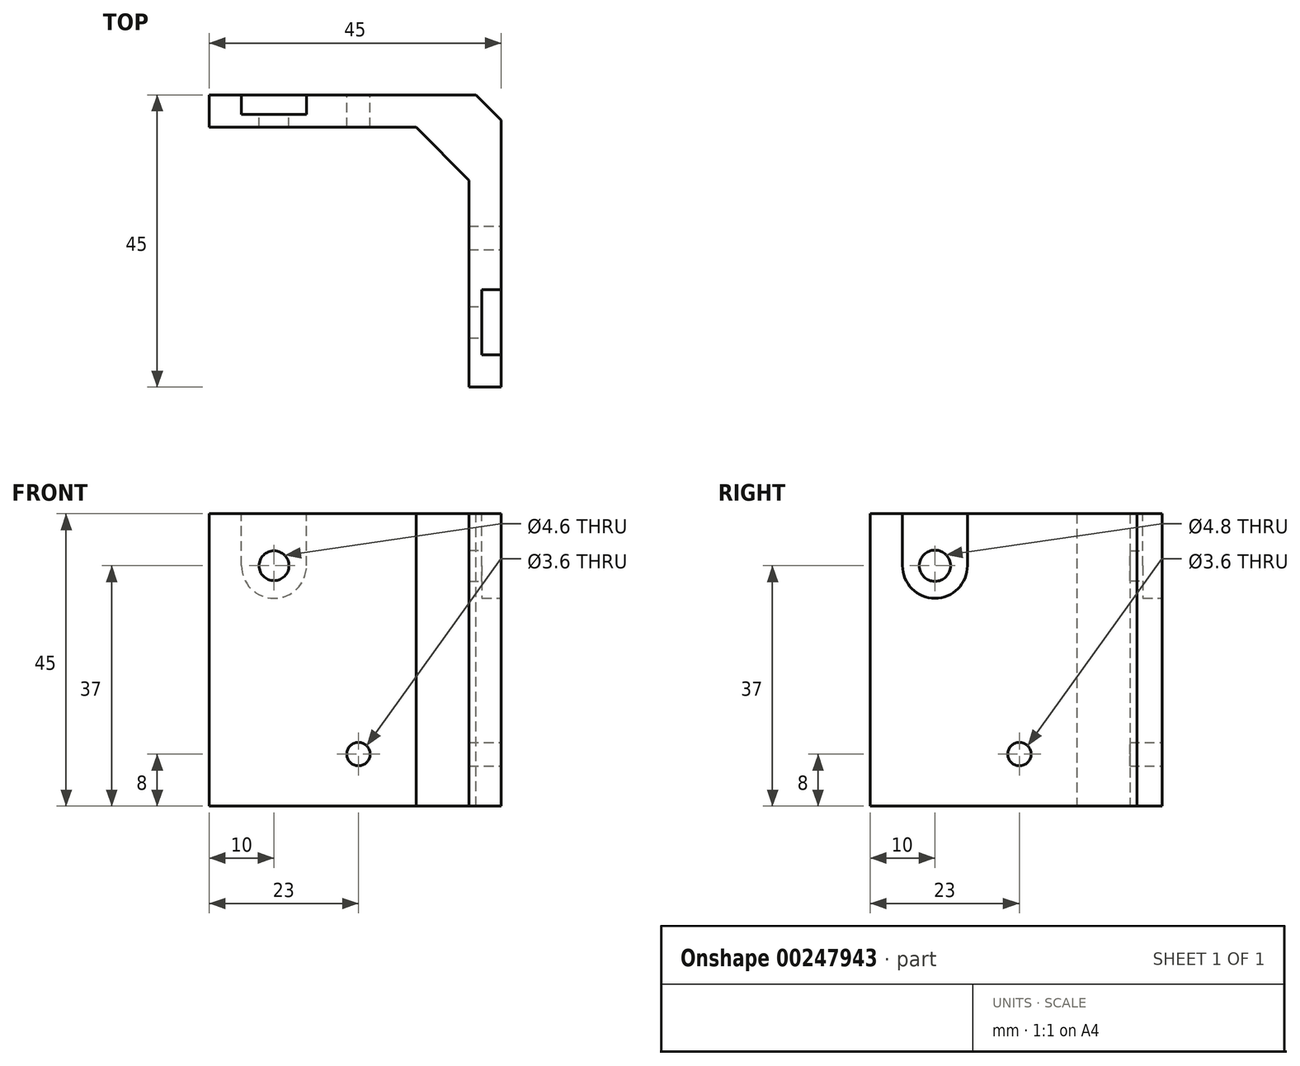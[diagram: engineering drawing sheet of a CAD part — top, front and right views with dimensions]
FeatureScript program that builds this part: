
annotation { "Feature Type Name" : "Feature", "Feature Type Description" : "" }
export const myFeature = defineFeature(function(context is Context, id is Id, definition is map)
    precondition{}
    {
        {
            var Q0;
            Q0=qCreatedBy(makeId("Top.planeOp"),FACE);
            var sketch = newSketch(context, id + "F0", { "sketchPlane" : qUnion([Q0])});
            skLineSegment(sketch, "E0.bottom", {"start": v(22.5, -22.5) * mm, "end": v(-22.5, -22.5) * mm});
            skLineSegment(sketch, "E0.top", {"start": v(22.5, 22.5) * mm, "end": v(-22.5, 22.5) * mm});
            skLineSegment(sketch, "E0.left", {"start": v(22.5, -22.5) * mm, "end": v(22.5, 22.5) * mm});
            skLineSegment(sketch, "E0.right", {"start": v(-22.5, -22.5) * mm, "end": v(-22.5, 22.5) * mm});
            skPoint(sketch, "E0.middle", {"position": v(0, 0) * mm});
            skSolve(sketch);
        }
        {
            var Q0;
            Q0 = qSketchRegion(id + "F0", true);
            extrude(context, id + "F1", {"entities" : qUnion([Q0]), "depth" : 5 * mm});
        }
        {
            var Q0;
            Q0=makeQuery(id+"F1.opExtrude","CAP_FACE",FACE,{"disambiguationData":[OSD([sQuery(id+"F0.wireOp",EDGE,"E0.bottom"),sQuery(id+"F0.wireOp",EDGE,"E0.top"),sQuery(id+"F0.wireOp",EDGE,"E0.left"),sQuery(id+"F0.wireOp",EDGE,"E0.right")])],"isStart":false});
            var sketch = newSketch(context, id + "F2", { "sketchPlane" : qUnion([Q0])});
            skLineSegment(sketch, "E1.bottom", {"start": v(-22.5, 22.5) * mm, "end": v(22.5, 22.5) * mm});
            skLineSegment(sketch, "E1.top", {"start": v(-22.5, 17.5) * mm, "end": v(22.5, 17.5) * mm});
            skLineSegment(sketch, "E1.left", {"start": v(-22.5, 22.5) * mm, "end": v(-22.5, 17.5) * mm});
            skLineSegment(sketch, "E1.right", {"start": v(22.5, 22.5) * mm, "end": v(22.5, 17.5) * mm});
            skSolve(sketch);
        }
        {
            var Q0;
            Q0=makeQuery(id+"F2.imprint","IMPRINT",FACE,{"disambiguationData":[TD([[makeQuery(id+"F2.imprint","IMPRINT",EDGE,{"derivedFrom":sQuery(id+"F2.wireOp",EDGE,"E1.bottom")}),1.0]])]});
            extrude(context, id + "F3", {"entities" : qUnion([Q0]), "operationType" : NewBodyOperationType.ADD, "depth" : 40 * mm});
        }
        {
            var Q0;
            Q0=makeQuery(id+"F3.boolean.opBoolean","MERGE",FACE,{"derivedFrom":[makeQuery(id+"F1.opExtrude","SWEPT_FACE",FACE,{"disambiguationData":[OSD([sQuery(id+"F0.wireOp",EDGE,"E0.right")])]}),makeQuery(id+"F3.opExtrude","SWEPT_FACE",FACE,{"disambiguationData":[OSD([sQuery(id+"F2.wireOp",EDGE,"E1.left")])]})]});
            var sketch = newSketch(context, id + "F4", { "sketchPlane" : qUnion([Q0])});
            skLineSegment(sketch, "E2.0", {"start": v(-17.5, 45) * mm, "end": v(-17.5, 5) * mm});
            skLineSegment(sketch, "E3.0", {"start": v(22.5, 5) * mm, "end": v(-17.5, 5) * mm});
            skLineSegment(sketch, "E4", {"start": v(-17.5, 13.13) * mm, "end": v(-9.37, 5) * mm});
            skSolve(sketch);
        }
        {
            var Q0;
            Q0 = qSketchRegion(id + "F4", true);
            var Q1;
            Q1=makeQuery(id+"F3.boolean.opBoolean","MERGE",FACE,{"derivedFrom":[makeQuery(id+"F1.opExtrude","SWEPT_FACE",FACE,{"disambiguationData":[OSD([sQuery(id+"F0.wireOp",EDGE,"E0.left")])]}),makeQuery(id+"F3.opExtrude","SWEPT_FACE",FACE,{"disambiguationData":[OSD([sQuery(id+"F2.wireOp",EDGE,"E1.right")])]})]});
            extrude(context, id + "F5", {"entities" : qUnion([Q0]), "operationType" : NewBodyOperationType.ADD, "endBound" : BoundingType.UP_TO_SURFACE, "oppositeDirection" : true, "endBoundEntityFace" : qUnion([Q1]), "depth" : 25 * mm});
        }
        {
            var Q0;
            Q0=makeQuery(id+"F5.boolean.opBoolean","MERGE",FACE,{"derivedFrom":[makeQuery(id+"F3.boolean.opBoolean","MERGE",FACE,{"derivedFrom":[makeQuery(id+"F1.opExtrude","SWEPT_FACE",FACE,{"disambiguationData":[OSD([sQuery(id+"F0.wireOp",EDGE,"E0.left")])]}),makeQuery(id+"F3.opExtrude","SWEPT_FACE",FACE,{"disambiguationData":[OSD([sQuery(id+"F2.wireOp",EDGE,"E1.right")])]})]}),makeQuery(id+"F5.opExtrude","CAP_FACE",FACE,{"disambiguationData":[OSD([sQuery(id+"F4.wireOp",EDGE,"E2.0"),sQuery(id+"F4.wireOp",EDGE,"E3.0"),sQuery(id+"F4.wireOp",EDGE,"E4")])],"isStart":false})]});
            var sketch = newSketch(context, id + "F6", { "sketchPlane" : qUnion([Q0])});
            skLineSegment(sketch, "E5", {"start": v(22.5, 0) * mm, "end": v(22.5, 3.89) * mm});
            skLineSegment(sketch, "E6", {"start": v(22.5, 3.89) * mm, "end": v(18.61, 0) * mm});
            skLineSegment(sketch, "E7", {"start": v(18.61, 0) * mm, "end": v(22.5, 0) * mm});
            skSolve(sketch);
        }
        {
            var Q0;
            Q0 = qSketchRegion(id + "F6", true);
            extrude(context, id + "F7", {"entities" : qUnion([Q0]), "operationType" : NewBodyOperationType.REMOVE, "endBound" : BoundingType.THROUGH_ALL, "oppositeDirection" : true, "depth" : 25 * mm});
        }
        {
            assignVariable(context, id + "F8", {"name" : "HoleDistFromEdge", "anyValue" : 8});
        }
        {
            var Q0;
            Q0=makeQuery(id+"F3.boolean.opBoolean","MERGE",FACE,{"derivedFrom":[makeQuery(id+"F1.opExtrude","SWEPT_FACE",FACE,{"disambiguationData":[OSD([sQuery(id+"F0.wireOp",EDGE,"E0.top")])]}),makeQuery(id+"F3.opExtrude","SWEPT_FACE",FACE,{"disambiguationData":[OSD([sQuery(id+"F2.wireOp",EDGE,"E1.bottom")])]})]});
            var sketch = newSketch(context, id + "F9", { "sketchPlane" : qUnion([Q0])});
            skPoint(sketch, "E8.0", {"position": v(22.5, 0) * mm});
            skLineSegment(sketch, "E9", {"start": v(22.5, 0) * mm, "end": v(22.5, 22) * mm, "construction": true});
            skLineSegment(sketch, "E10", {"start": v(22.5, 22) * mm, "end": v(14.5, 22) * mm, "construction": true});
            skCircle(sketch, "E11", {"center": v(14.5, 22) * mm, "radius": 1.8 * mm});
            skPoint(sketch, "E12.0", {"position": v(-22.5, 0) * mm});
            skLineSegment(sketch, "E13", {"start": v(-22.5, 0) * mm, "end": v(-22.5, 35) * mm, "construction": true});
            skLineSegment(sketch, "E14", {"start": v(-22.5, 35) * mm, "end": v(-14.5, 35) * mm, "construction": true});
            skCircle(sketch, "E15", {"center": v(-14.5, 35) * mm, "radius": 2.3 * mm});
            skSolve(sketch);
        }
        {
            var Q0;
            Q0 = qSketchRegion(id + "F9", true);
            extrude(context, id + "F10", {"entities" : qUnion([Q0]), "operationType" : NewBodyOperationType.REMOVE, "endBound" : BoundingType.THROUGH_ALL, "oppositeDirection" : true, "depth" : 25 * mm});
        }
        {
            var Q0;
            Q0=makeQuery(id+"F1.opExtrude","CAP_FACE",FACE,{"disambiguationData":[OSD([sQuery(id+"F0.wireOp",EDGE,"E0.bottom"),sQuery(id+"F0.wireOp",EDGE,"E0.top"),sQuery(id+"F0.wireOp",EDGE,"E0.left"),sQuery(id+"F0.wireOp",EDGE,"E0.right")])],"isStart":true});
            var sketch = newSketch(context, id + "F11", { "sketchPlane" : qUnion([Q0])});
            skPoint(sketch, "E16.0", {"position": v(22.5, -22.5) * mm});
            skPoint(sketch, "E17.0", {"position": v(-22.5, -22.5) * mm});
            skLineSegment(sketch, "E18", {"start": v(-22.5, -22.5) * mm, "end": v(-22.5, -0.5) * mm, "construction": true});
            skLineSegment(sketch, "E19", {"start": v(22.5, -22.5) * mm, "end": v(22.5, 12.5) * mm, "construction": true});
            skLineSegment(sketch, "E20", {"start": v(22.5, 12.5) * mm, "end": v(14.5, 12.5) * mm, "construction": true});
            skLineSegment(sketch, "E21", {"start": v(-22.5, -0.5) * mm, "end": v(-14.5, -0.5) * mm, "construction": true});
            skCircle(sketch, "E22", {"center": v(-14.5, -0.5) * mm, "radius": 1.8 * mm});
            skCircle(sketch, "E23", {"center": v(14.5, 12.5) * mm, "radius": 2.4 * mm});
            skSolve(sketch);
        }
        {
            var Q0;
            Q0=makeQuery(id+"F11.imprint","IMPRINT",FACE,{"disambiguationData":[TD([[makeQuery(id+"F11.imprint","IMPRINT",EDGE,{"derivedFrom":sQuery(id+"F11.wireOp",EDGE,"E23")}),1.0]])]});
            var Q1;
            Q1=makeQuery(id+"F11.imprint","IMPRINT",FACE,{"disambiguationData":[TD([[makeQuery(id+"F11.imprint","IMPRINT",EDGE,{"derivedFrom":sQuery(id+"F11.wireOp",EDGE,"E22")}),1.0]])]});
            extrude(context, id + "F12", {"entities" : qUnion([Q0, Q1]), "operationType" : NewBodyOperationType.REMOVE, "endBound" : BoundingType.THROUGH_ALL, "oppositeDirection" : true, "depth" : 25 * mm});
        }
        {
            var Q0;
            Q0=makeQuery(id+"F5.boolean.opBoolean","MERGE",FACE,{"derivedFrom":[makeQuery(id+"F3.boolean.opBoolean","MERGE",FACE,{"derivedFrom":[makeQuery(id+"F1.opExtrude","SWEPT_FACE",FACE,{"disambiguationData":[OSD([sQuery(id+"F0.wireOp",EDGE,"E0.left")])]}),makeQuery(id+"F3.opExtrude","SWEPT_FACE",FACE,{"disambiguationData":[OSD([sQuery(id+"F2.wireOp",EDGE,"E1.right")])]})]}),makeQuery(id+"F5.opExtrude","CAP_FACE",FACE,{"disambiguationData":[OSD([sQuery(id+"F4.wireOp",EDGE,"E2.0"),sQuery(id+"F4.wireOp",EDGE,"E3.0"),sQuery(id+"F4.wireOp",EDGE,"E4")])],"isStart":false})]});
            var sketch = newSketch(context, id + "F13", { "sketchPlane" : qUnion([Q0])});
            skLineSegment(sketch, "E24.0", {"start": v(-10.1, 0) * mm, "end": v(-14.9, 0) * mm, "construction": true});
            skLineSegment(sketch, "E25.bottom", {"start": v(-17.5, 0) * mm, "end": v(-7.5, 0) * mm});
            skLineSegment(sketch, "E25.top", {"start": v(-17.5, 3) * mm, "end": v(-7.5, 3) * mm});
            skLineSegment(sketch, "E25.left", {"start": v(-17.5, 0) * mm, "end": v(-17.5, 3) * mm});
            skLineSegment(sketch, "E25.right", {"start": v(-7.5, 0) * mm, "end": v(-7.5, 3) * mm});
            skPoint(sketch, "E26", {"position": v(-12.5, 0) * mm});
            skLineSegment(sketch, "E27", {"start": v(13.43, 9.07) * mm, "end": v(20.56, 1.94) * mm, "construction": true});
            skLineSegment(sketch, "E28.MirrorCS", {"start": v(19.5, 40) * mm, "end": v(19.5, 30) * mm});
            skLineSegment(sketch, "E29.MirrorCS", {"start": v(22.5, 40) * mm, "end": v(19.5, 40) * mm});
            skLineSegment(sketch, "E30.MirrorCS", {"start": v(22.5, 30) * mm, "end": v(19.5, 30) * mm});
            skLineSegment(sketch, "E31.MirrorCS", {"start": v(22.5, 40) * mm, "end": v(22.5, 30) * mm});
            skSolve(sketch);
        }
        {
            var Q0;
            Q0 = qSketchRegion(id + "F13", true);
            extrude(context, id + "F14", {"entities" : qUnion([Q0]), "operationType" : NewBodyOperationType.REMOVE, "oppositeDirection" : true, "depth" : (getVariable(context, 'HoleDistFromEdge') + 5) * mm});
        }
        {
            var Q0;
            Q0=makeQuery(id+"F14.boolean.opBoolean","COPY",EDGE,{"derivedFrom":makeQuery(id+"F14.opExtrude","CAP_EDGE",EDGE,{"disambiguationData":[OSD([sQuery(id+"F13.wireOp",EDGE,"E25.left")])],"isStart":false})});
            var Q1;
            Q1=makeQuery(id+"F14.boolean.opBoolean","COPY",EDGE,{"derivedFrom":makeQuery(id+"F14.opExtrude","CAP_EDGE",EDGE,{"disambiguationData":[OSD([sQuery(id+"F13.wireOp",EDGE,"E25.right")])],"isStart":false})});
            var Q2;
            Q2=makeQuery(id+"F14.boolean.opBoolean","COPY",EDGE,{"derivedFrom":makeQuery(id+"F14.opExtrude","CAP_EDGE",EDGE,{"disambiguationData":[OSD([sQuery(id+"F13.wireOp",EDGE,"E30.MirrorCS")])],"isStart":false})});
            var Q3;
            Q3=makeQuery(id+"F14.boolean.opBoolean","COPY",EDGE,{"derivedFrom":makeQuery(id+"F14.opExtrude","CAP_EDGE",EDGE,{"disambiguationData":[OSD([sQuery(id+"F13.wireOp",EDGE,"E29.MirrorCS")])],"isStart":false})});
            fillet(context, id + "F15", {"entities" : qUnion([Q0, Q1, Q2, Q3]), "radius" : 5 * mm, "tangentPropagation" : true, "allowEdgeOverflow" : false});
        }
        {
            var Q0;
            Q0=makeQuery(id+"F1.opExtrude","SWEPT_BODY",BODY,{"disambiguationData":[OSD([sQuery(id+"F0.wireOp",EDGE,"E0.bottom"),sQuery(id+"F0.wireOp",EDGE,"E0.top"),sQuery(id+"F0.wireOp",EDGE,"E0.left"),sQuery(id+"F0.wireOp",EDGE,"E0.right")])]});
            var Q1;
            Q1=makeQuery(id+"F1.opExtrude","CAP_EDGE",EDGE,{"disambiguationData":[OSD([sQuery(id+"F0.wireOp",EDGE,"E0.right")])],"isStart":true});
            transform(context, id + "F16", {"entities" : qUnion([Q0]), "transformType" : TransformType.ROTATION, "transformAxis" : qUnion([Q1]), "angle" : 90 * degree, "oppositeDirection" : true, "makeCopy" : false});
        }
        {
            var Q0;
            Q0=makeQuery(id+"F1.opExtrude","SWEPT_BODY",BODY,{"disambiguationData":[OSD([sQuery(id+"F0.wireOp",EDGE,"E0.bottom"),sQuery(id+"F0.wireOp",EDGE,"E0.top"),sQuery(id+"F0.wireOp",EDGE,"E0.left"),sQuery(id+"F0.wireOp",EDGE,"E0.right")])]});
            transform(context, id + "F17", {"entities" : qUnion([Q0]), "transformType" : TransformType.TRANSLATION_3D, "dx" : 40 * mm, "dy" : 0 * mm, "dz" : 0 * mm, "makeCopy" : false});
        }
    });
